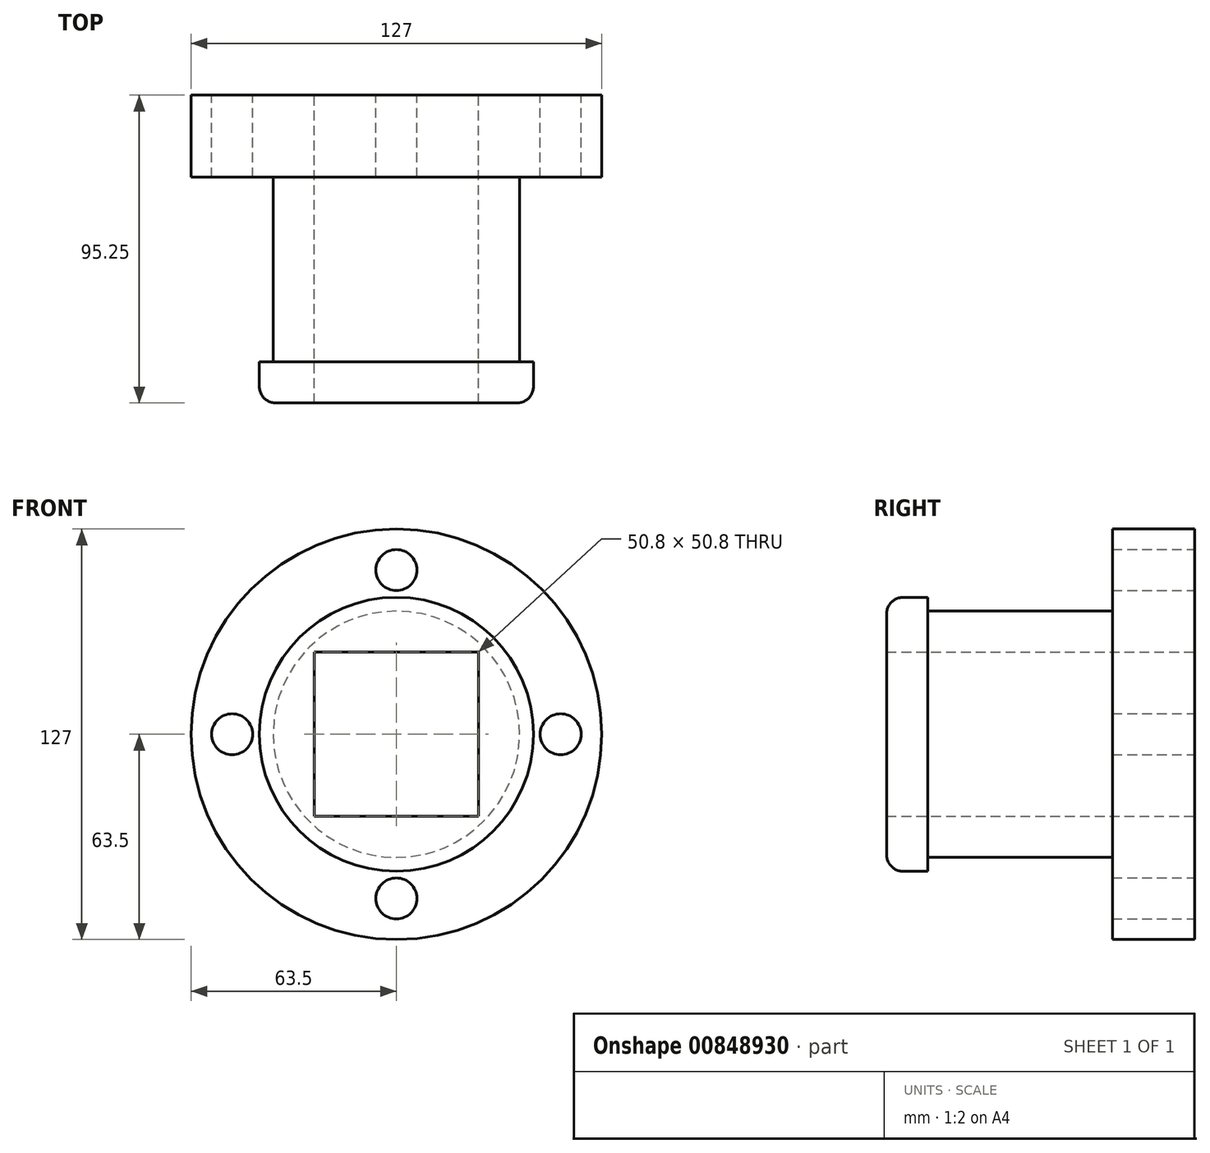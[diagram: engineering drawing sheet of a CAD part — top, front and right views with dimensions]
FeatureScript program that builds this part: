
annotation { "Feature Type Name" : "Feature", "Feature Type Description" : "" }
export const myFeature = defineFeature(function(context is Context, id is Id, definition is map)
    precondition{}
    {
        {
            var Q0;
            Q0=qCreatedBy(makeId("Front.planeOp"),FACE);
            var sketch = newSketch(context, id + "F0", { "sketchPlane" : qUnion([Q0])});
            skPoint(sketch, "E0.middle", {"position": v(0, 0) * mm});
            skCircle(sketch, "E1", {"center": v(0, 0) * mm, "radius": 38.1 * mm});
            skCircle(sketch, "E2", {"center": v(0, 0) * mm, "radius": 42.38 * mm});
            skPoint(sketch, "E0.bottom.end.orphan", {"position": v(-44.9, 44.9) * mm});
            skLineSegment(sketch, "E3.bottom", {"start": v(25.4, 25.4) * mm, "end": v(-25.4, 25.4) * mm});
            skLineSegment(sketch, "E3.top", {"start": v(25.4, -25.4) * mm, "end": v(-25.4, -25.4) * mm});
            skLineSegment(sketch, "E3.left", {"start": v(25.4, 25.4) * mm, "end": v(25.4, -25.4) * mm});
            skLineSegment(sketch, "E3.right", {"start": v(-25.4, 25.4) * mm, "end": v(-25.4, -25.4) * mm});
            skSolve(sketch);
        }
        {
            var Q0;
            Q0 = qSketchRegion(id + "F0", true);
            var Q1;
            Q1=makeQuery(id+"F0.imprint","IMPRINT",FACE,{"disambiguationData":[TD([[makeQuery(id+"F0.imprint","IMPRINT",EDGE,{"derivedFrom":sQuery(id+"F0.wireOp",EDGE,"E1")}),-1.0]])]});
            var Q2;
            Q2=makeQuery(id+"F0.imprint","IMPRINT",FACE,{"disambiguationData":[TD([[makeQuery(id+"F0.imprint","IMPRINT",EDGE,{"derivedFrom":sQuery(id+"F0.wireOp",EDGE,"E1")}),1.0]])]});
            extrude(context, id + "F1", {"entities" : qUnion([Q0, Q1, Q2]), "depth" : 12.7 * mm, "offsetDistance" : 25.4 * mm});
        }
        {
            var Q0;
            Q0=makeQuery(id+"F1.opExtrude","CAP_FACE",FACE,{"disambiguationData":[OSD([sQuery(id+"F0.wireOp",EDGE,"E2"),sQuery(id+"F0.wireOp",EDGE,"9ddd9JLH-LeJv-IsP2-ven9-nSaOeduKehbh"),sQuery(id+"F0.wireOp",EDGE,"rqvqu0k0-RUg7-hCii-iD4H-BKWiAHTwuaUj"),sQuery(id+"F0.wireOp",EDGE,"24bb96e7-fb2d-4305-9cd9-792aa5656be3.trimOffspring"),sQuery(id+"F0.wireOp",EDGE,"2a13722d-d2c6-4950-8d9f-c86fb685b7fd.trimOffspring"),sQuery(id+"F0.wireOp",EDGE,"CVXVzHpp-sL4r-Hah5-Jp8G-c1i4ZKY5sqAr"),sQuery(id+"F0.wireOp",EDGE,"E3.bottom"),sQuery(id+"F0.wireOp",EDGE,"E3.top"),sQuery(id+"F0.wireOp",EDGE,"E3.left"),sQuery(id+"F0.wireOp",EDGE,"E3.right")])],"isStart":true});
            var sketch = newSketch(context, id + "F2", { "sketchPlane" : qUnion([Q0])});
            skCircle(sketch, "E4", {"center": v(0, 0) * mm, "radius": 38.1 * mm});
            skSolve(sketch);
        }
        {
            var Q0;
            Q0=makeQuery(id+"F2.imprint","IMPRINT",FACE,{"disambiguationData":[TD([[makeQuery(id+"F2.imprint","IMPRINT",EDGE,{"derivedFrom":sQuery(id+"F2.wireOp",EDGE,"E4")}),1.0]])]});
            extrude(context, id + "F3", {"entities" : qUnion([Q0]), "operationType" : NewBodyOperationType.ADD, "depth" : 57.15 * mm, "offsetDistance" : 25.4 * mm});
        }
        {
            var Q0;
            Q0=makeQuery(id+"F3.opExtrude","CAP_FACE",FACE,{"disambiguationData":[OSD([sQuery(id+"F0.wireOp",EDGE,"E3.bottom"),sQuery(id+"F0.wireOp",EDGE,"E3.top"),sQuery(id+"F0.wireOp",EDGE,"E3.left"),sQuery(id+"F0.wireOp",EDGE,"E3.right"),sQuery(id+"F2.wireOp",EDGE,"E4")])],"isStart":false});
            var sketch = newSketch(context, id + "F4", { "sketchPlane" : qUnion([Q0])});
            skCircle(sketch, "E5", {"center": v(0, 0) * mm, "radius": 63.5 * mm});
            skSolve(sketch);
        }
        {
            var Q0;
            Q0=makeQuery(id+"F4.imprint","IMPRINT",FACE,{"disambiguationData":[TD([[makeQuery(id+"F4.imprint","IMPRINT",EDGE,{"derivedFrom":sQuery(id+"F4.wireOp",EDGE,"E5")}),1.0]])]});
            var Q1;
            Q1=makeQuery(id+"F4.imprint","IMPRINT",FACE,{"disambiguationData":[TD([[makeQuery(id+"F4.imprint","IMPRINT",EDGE,{"derivedFrom":makeQuery(id+"F3.opExtrude","CAP_EDGE",EDGE,{"disambiguationData":[OSD([sQuery(id+"F2.wireOp",EDGE,"E4")])],"isStart":false})}),1.0]])]});
            extrude(context, id + "F5", {"entities" : qUnion([Q0, Q1]), "operationType" : NewBodyOperationType.ADD, "depth" : 25.4 * mm, "offsetDistance" : 25.4 * mm});
        }
        {
            var Q0;
            Q0=makeQuery(id+"F5.opExtrude","CAP_FACE",FACE,{"disambiguationData":[OSD([sQuery(id+"F0.wireOp",EDGE,"E3.bottom"),sQuery(id+"F0.wireOp",EDGE,"E3.top"),sQuery(id+"F0.wireOp",EDGE,"E3.left"),sQuery(id+"F0.wireOp",EDGE,"E3.right"),sQuery(id+"F4.wireOp",EDGE,"E5")])],"isStart":false});
            var sketch = newSketch(context, id + "F6", { "sketchPlane" : qUnion([Q0])});
            skCircle(sketch, "E6", {"center": v(0, -50.8) * mm, "radius": 6.35 * mm});
            skPoint(sketch, "E7.endSnap0", {"position": v(-25.4, 0) * mm});
            skCircle(sketch, "E8", {"center": v(-50.8, 0) * mm, "radius": 6.35 * mm});
            skPoint(sketch, "E9.endSnap0", {"position": v(25.4, 0) * mm});
            skCircle(sketch, "E10", {"center": v(50.8, 0) * mm, "radius": 6.35 * mm});
            skPoint(sketch, "E11.endSnap0", {"position": v(0, 25.4) * mm});
            skCircle(sketch, "E12", {"center": v(0, 50.8) * mm, "radius": 6.35 * mm});
            skSolve(sketch);
        }
        {
            var Q0;
            Q0=makeQuery(id+"F6.imprint","IMPRINT",FACE,{"disambiguationData":[TD([[makeQuery(id+"F6.imprint","IMPRINT",EDGE,{"derivedFrom":sQuery(id+"F6.wireOp",EDGE,"E6")}),1.0]])]});
            var Q1;
            Q1=makeQuery(id+"F6.imprint","IMPRINT",FACE,{"disambiguationData":[TD([[makeQuery(id+"F6.imprint","IMPRINT",EDGE,{"derivedFrom":sQuery(id+"F6.wireOp",EDGE,"E8")}),1.0]])]});
            var Q2;
            Q2=makeQuery(id+"F6.imprint","IMPRINT",FACE,{"disambiguationData":[TD([[makeQuery(id+"F6.imprint","IMPRINT",EDGE,{"derivedFrom":sQuery(id+"F6.wireOp",EDGE,"E12")}),1.0]])]});
            var Q3;
            Q3=makeQuery(id+"F6.imprint","IMPRINT",FACE,{"disambiguationData":[TD([[makeQuery(id+"F6.imprint","IMPRINT",EDGE,{"derivedFrom":sQuery(id+"F6.wireOp",EDGE,"E10")}),1.0]])]});
            extrude(context, id + "F7", {"entities" : qUnion([Q0, Q1, Q2, Q3]), "operationType" : NewBodyOperationType.REMOVE, "oppositeDirection" : true, "depth" : 38.1 * mm, "offsetDistance" : 25.4 * mm});
        }
        {
            var Q0;
            Q0=makeQuery(id+"F1.opExtrude","CAP_EDGE",EDGE,{"disambiguationData":[OSD([sQuery(id+"F0.wireOp",EDGE,"E2")])],"isStart":false});
            fillet(context, id + "F8", {"entities" : qUnion([Q0]), "radius" : 5.08 * mm, "tangentPropagation" : true, "allowEdgeOverflow" : false});
        }
    });
